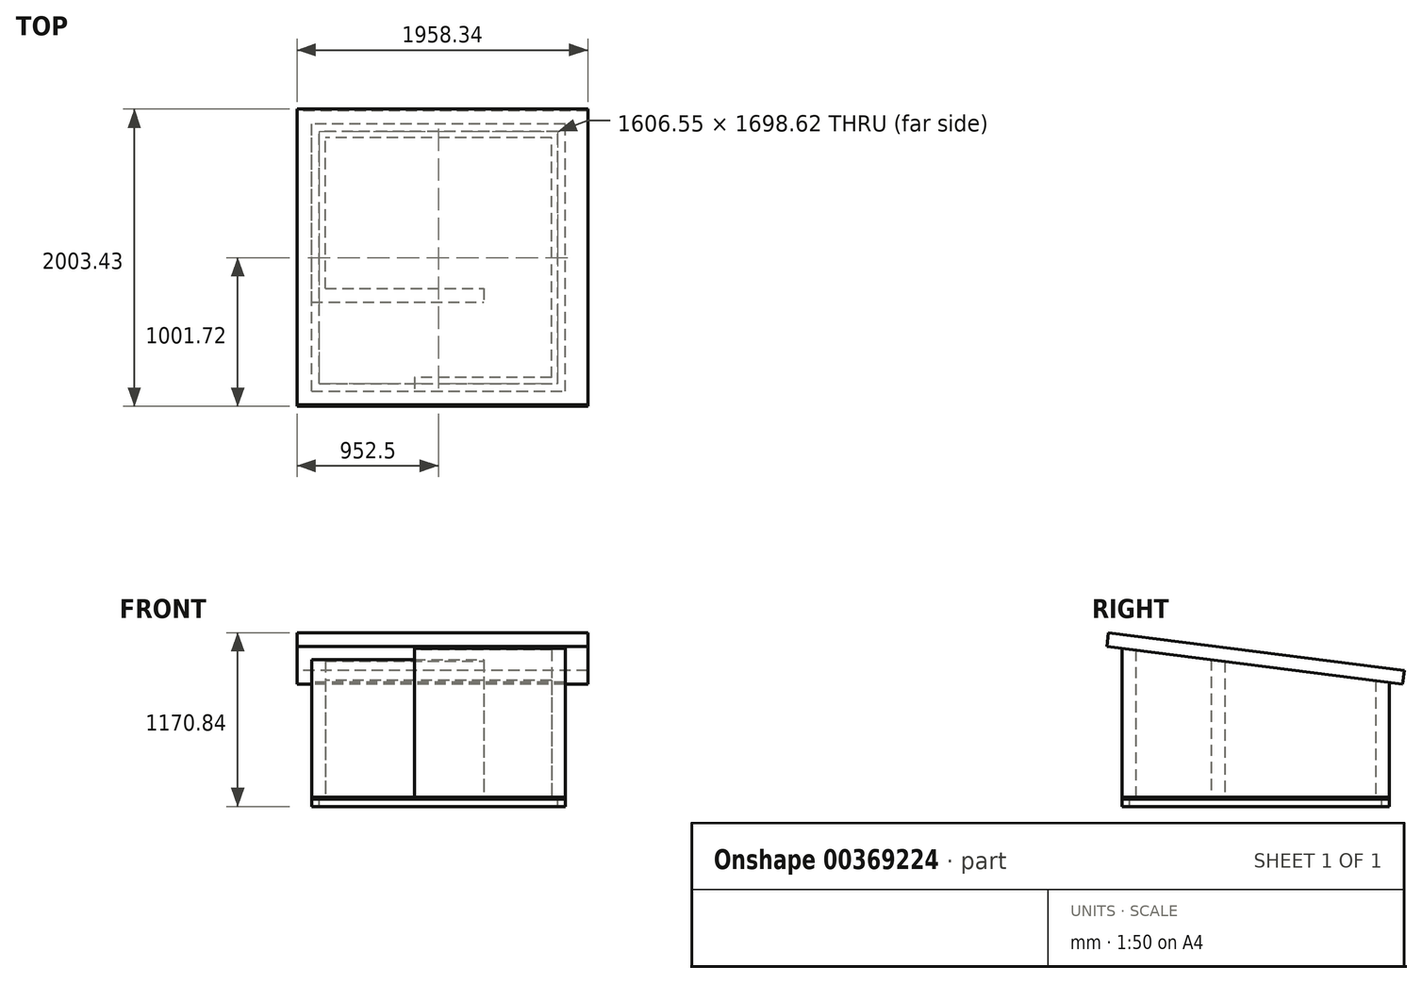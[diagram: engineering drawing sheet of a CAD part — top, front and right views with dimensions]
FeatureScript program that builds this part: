
annotation { "Feature Type Name" : "Feature", "Feature Type Description" : "" }
export const myFeature = defineFeature(function(context is Context, id is Id, definition is map)
    precondition{}
    {
        {
            var Q0;
            Q0=qCreatedBy(makeId("Top.planeOp"),FACE);
            var sketch = newSketch(context, id + "F0", { "sketchPlane" : qUnion([Q0])});
            skLineSegment(sketch, "E0.top", {"start": v(549.28, 1200.15) * mm, "end": v(-1158.87, 1200.15) * mm});
            skLineSegment(sketch, "E0.left", {"start": v(549.27, -600.08) * mm, "end": v(549.28, 1200.15) * mm});
            skLineSegment(sketch, "E0.right", {"start": v(-1158.88, 0) * mm, "end": v(-1158.87, 1200.15) * mm});
            skPoint(sketch, "E0.middle", {"position": v(0, 0) * mm});
            skLineSegment(sketch, "E1", {"start": v(-1158.88, 0) * mm, "end": v(0, 0) * mm});
            skLineSegment(sketch, "E2.0", {"start": v(-1066.8, 92.08) * mm, "end": v(0, 92.08) * mm});
            skLineSegment(sketch, "E2.2", {"start": v(457.2, -508) * mm, "end": v(457.2, 1108.07) * mm});
            skLineSegment(sketch, "E2.3", {"start": v(457.2, 1108.07) * mm, "end": v(-1066.8, 1108.08) * mm});
            skLineSegment(sketch, "E2.4", {"start": v(-1066.8, 92.07) * mm, "end": v(-1066.8, 1108.08) * mm});
            skLineSegment(sketch, "E3", {"start": v(0, 92.08) * mm, "end": v(0, 0) * mm});
            skLineSegment(sketch, "E4", {"start": v(-466.73, -600.08) * mm, "end": v(549.27, -600.08) * mm});
            skLineSegment(sketch, "E5", {"start": v(457.2, -508) * mm, "end": v(-466.73, -508) * mm});
            skLineSegment(sketch, "E6.trimOffspring", {"start": v(-466.73, -508) * mm, "end": v(-466.73, -600.08) * mm});
            skSolve(sketch);
        }
        {
            var Q0;
            Q0=qCreatedBy(makeId("Right.planeOp"),FACE);
            var sketch = newSketch(context, id + "F1", { "sketchPlane" : qUnion([Q0])});
            skLineSegment(sketch, "E7", {"start": v(-701.68, 1016) * mm, "end": v(1290.1, 762) * mm});
            skLineSegment(sketch, "E8", {"start": v(-701.68, 1016) * mm, "end": v(-690.03, 1107.34) * mm});
            skLineSegment(sketch, "E9", {"start": v(-690.03, 1107.34) * mm, "end": v(1301.75, 853.34) * mm});
            skLineSegment(sketch, "E10", {"start": v(1290.1, 762) * mm, "end": v(1301.75, 853.34) * mm});
            skSolve(sketch);
        }
        {
            var Q0;
            Q0=makeQuery(id+"F1.imprint","IMPRINT",FACE,{"disambiguationData":[TD([[makeQuery(id+"F1.imprint","IMPRINT",EDGE,{"derivedFrom":sQuery(id+"F1.wireOp",EDGE,"E7")}),1.0]])]});
            extrude(context, id + "F2", {"entities" : qUnion([Q0]), "depth" : 701.04 * mm, "hasSecondDirection" : true, "secondDirectionOppositeDirection" : true, "secondDirectionDepth" : 1257.3 * mm});
        }
        {
            var Q0;
            Q0=qSketchRegion(id+"F0",true);
            var Q1;
            Q1=makeQuery(id+"F2.opExtrude","SWEPT_FACE",FACE,{"disambiguationData":[OSD([sQuery(id+"F1.wireOp",EDGE,"E7")])]});
            var Q2;
            Q2=makeQuery(id+"F2.opExtrude","SWEPT_BODY",BODY,{"disambiguationData":[OSD([sQuery(id+"F1.wireOp",EDGE,"E7"),sQuery(id+"F1.wireOp",EDGE,"E8"),sQuery(id+"F1.wireOp",EDGE,"E9"),sQuery(id+"F1.wireOp",EDGE,"E10")])]});
            extrude(context, id + "F3", {"entities" : qUnion([Q0]), "endBound" : BoundingType.UP_TO_SURFACE, "endBoundEntityFace" : qUnion([Q1]), "endBoundEntityBody" : qUnion([Q2]), "depth" : 25.4 * mm});
        }
        {
            var Q0;
            Q0=makeQuery(id+"F3.opExtrude","CAP_FACE",FACE,{"disambiguationData":[OSD([sQuery(id+"F0.wireOp",EDGE,"E0.top"),sQuery(id+"F0.wireOp",EDGE,"E0.left"),sQuery(id+"F0.wireOp",EDGE,"E0.right"),sQuery(id+"F0.wireOp",EDGE,"E1"),sQuery(id+"F0.wireOp",EDGE,"E2.0"),sQuery(id+"F0.wireOp",EDGE,"E2.2"),sQuery(id+"F0.wireOp",EDGE,"E2.3"),sQuery(id+"F0.wireOp",EDGE,"E2.4"),sQuery(id+"F0.wireOp",EDGE,"E3"),sQuery(id+"F0.wireOp",EDGE,"E4"),sQuery(id+"F0.wireOp",EDGE,"E5"),sQuery(id+"F0.wireOp",EDGE,"E6.trimOffspring")])],"isStart":true});
            var sketch = newSketch(context, id + "F4", { "sketchPlane" : qUnion([Q0])});
            skLineSegment(sketch, "E11", {"start": v(-1158.87, -1200.15) * mm, "end": v(549.28, -1200.15) * mm});
            skLineSegment(sketch, "E12", {"start": v(549.28, -1200.15) * mm, "end": v(549.28, 600.08) * mm});
            skLineSegment(sketch, "E13", {"start": v(549.27, 600.08) * mm, "end": v(-1158.88, 600.07) * mm});
            skPoint(sketch, "E13.endSnap0", {"position": v(-1158.87, -600.08) * mm});
            skLineSegment(sketch, "E14", {"start": v(-1158.88, 600.07) * mm, "end": v(-1158.87, -1200.15) * mm});
            skSolve(sketch);
        }
        {
            var Q0;
            Q0=qSketchRegion(id+"F4",true);
            extrude(context, id + "F5", {"entities" : qUnion([Q0]), "depth" : 12.7 * mm});
        }
        {
            var Q0;
            Q0=makeQuery(id+"F5.opExtrude","CAP_FACE",FACE,{"disambiguationData":[OSD([sQuery(id+"F4.wireOp",EDGE,"E11"),sQuery(id+"F4.wireOp",EDGE,"E12"),sQuery(id+"F4.wireOp",EDGE,"E13"),sQuery(id+"F4.wireOp",EDGE,"E14")])],"isStart":false});
            var sketch = newSketch(context, id + "F6", { "sketchPlane" : qUnion([Q0])});
            skLineSegment(sketch, "E15.0", {"start": v(-1158.88, 600.07) * mm, "end": v(-1158.87, -1200.15) * mm});
            skLineSegment(sketch, "E16.0", {"start": v(-1158.88, 600.08) * mm, "end": v(549.27, 600.08) * mm});
            skLineSegment(sketch, "E17.0", {"start": v(549.27, 600.08) * mm, "end": v(549.28, -1200.15) * mm});
            skLineSegment(sketch, "E18.0", {"start": v(-1108.08, 549.28) * mm, "end": v(-1108.07, -1149.35) * mm});
            skLineSegment(sketch, "E18.1", {"start": v(-1108.08, 549.28) * mm, "end": v(498.47, 549.28) * mm});
            skLineSegment(sketch, "E18.2", {"start": v(498.47, 549.28) * mm, "end": v(498.48, -1149.35) * mm});
            skLineSegment(sketch, "E18.3", {"start": v(498.48, -1149.35) * mm, "end": v(-1108.07, -1149.35) * mm});
            skSolve(sketch);
        }
        {
            var Q0;
            Q0=makeQuery(id+"F6.imprint","IMPRINT",FACE,{"disambiguationData":[TD([[makeQuery(id+"F6.imprint","IMPRINT",EDGE,{"derivedFrom":sQuery(id+"F6.wireOp",EDGE,"E15.0")}),1.0]])]});
            extrude(context, id + "F7", {"entities" : qUnion([Q0]), "depth" : 50.8 * mm});
        }
    });
